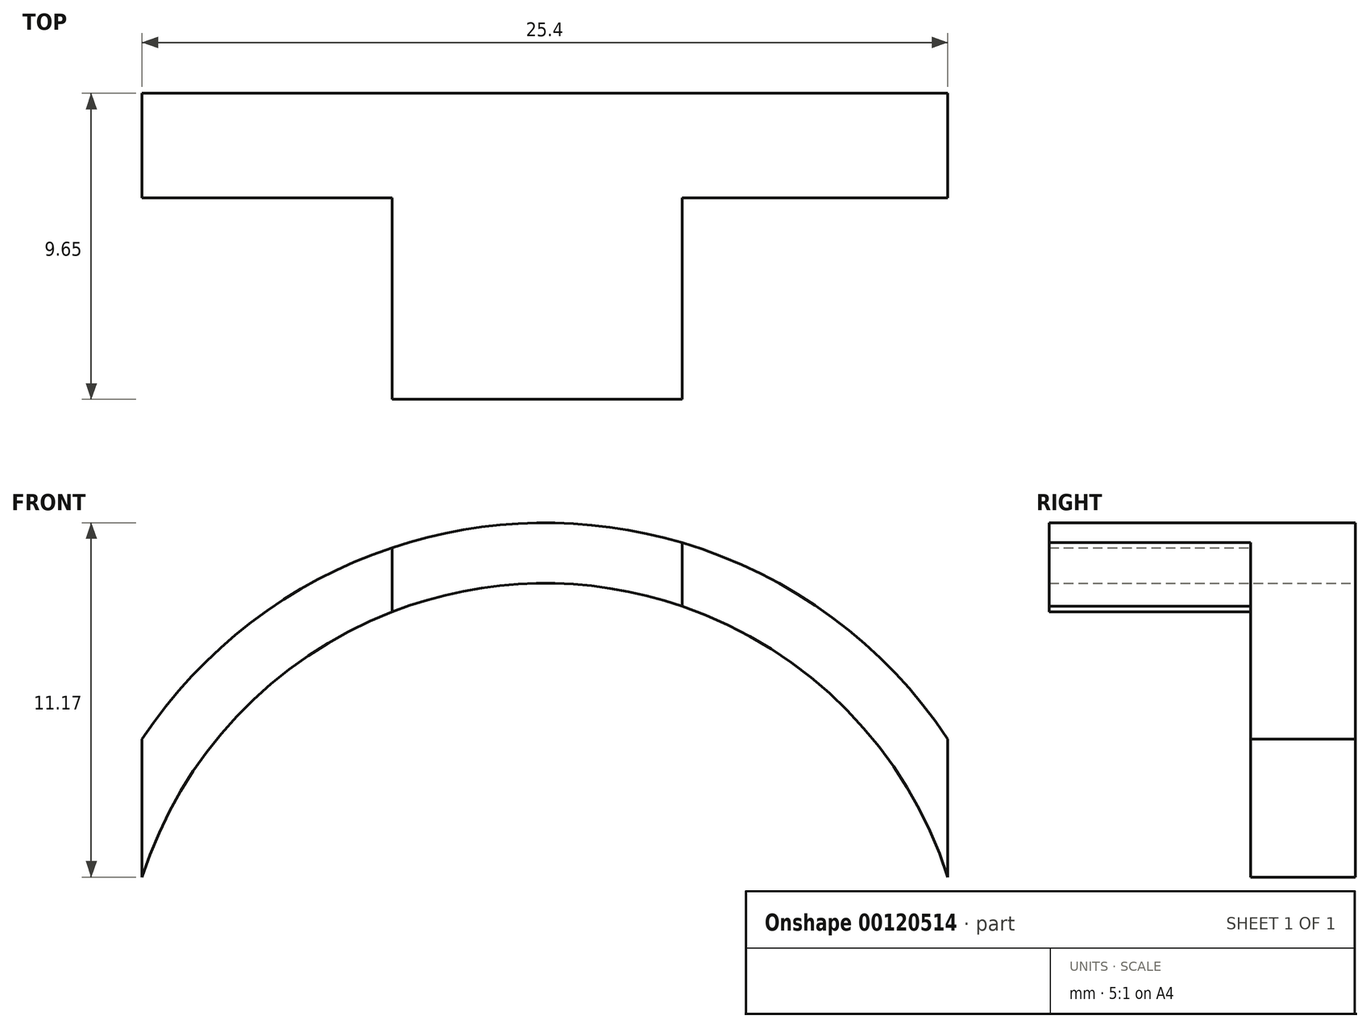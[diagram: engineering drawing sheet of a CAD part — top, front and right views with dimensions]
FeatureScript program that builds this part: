
annotation { "Feature Type Name" : "Feature", "Feature Type Description" : "" }
export const myFeature = defineFeature(function(context is Context, id is Id, definition is map)
    precondition{}
    {
        {
            var Q0;
            Q0=qCreatedBy(makeId("Front.planeOp"),FACE);
            var sketch = newSketch(context, id + "F0", { "sketchPlane" : qUnion([Q0])});
            skCircle(sketch, "E0", {"center": v(0, 0) * mm, "radius": 15.24 * mm});
            skCircle(sketch, "E1", {"center": v(0, 0) * mm, "radius": 13.34 * mm});
            skLineSegment(sketch, "E2.bottom", {"start": v(12.7, 0) * mm, "end": v(-12.7, 0) * mm});
            skLineSegment(sketch, "E2.top", {"start": v(12.7, 25.4) * mm, "end": v(-12.7, 25.4) * mm});
            skLineSegment(sketch, "E2.left", {"start": v(12.7, 0) * mm, "end": v(12.7, 25.4) * mm});
            skLineSegment(sketch, "E2.right", {"start": v(-12.7, 0) * mm, "end": v(-12.7, 25.4) * mm});
            skSolve(sketch);
        }
        {
            var Q0;
            {var subQ0=sQuery(id+"F0.wireOp",EDGE,"E2.left");var subQ1=sQuery(id+"F0.wireOp",EDGE,"E0");var subQ2=makeQuery(id+"F0.imprint","INTERSECT",VERTEX,{"derivedFrom":[subQ1,subQ0]});Q0=makeQuery(id+"F0.imprint","IMPRINT",FACE,{"disambiguationData":[TD([[makeQuery(id+"F0.imprint","IMPRINT",EDGE,{"disambiguationData":[TD([[subQ2,-1.0]])],"derivedFrom":subQ1}),1.0]])]});}
            extrude(context, id + "F1", {"entities" : qUnion([Q0]), "depth" : 3.3 * mm});
        }
        {
            var Q0;
            Q0=makeQuery(id+"F1.opExtrude","CAP_FACE",FACE,{"disambiguationData":[OSD([sQuery(id+"F0.wireOp",EDGE,"E0"),sQuery(id+"F0.wireOp",EDGE,"E1"),sQuery(id+"F0.wireOp",EDGE,"E2.left"),sQuery(id+"F0.wireOp",EDGE,"E2.right")])],"isStart":false});
            var sketch = newSketch(context, id + "F2", { "sketchPlane" : qUnion([Q0])});
            skLineSegment(sketch, "E3.bottom", {"start": v(-4.82, 15.24) * mm, "end": v(4.32, 15.24) * mm});
            skLineSegment(sketch, "E3.top", {"start": v(-4.82, -9.06) * mm, "end": v(4.32, -9.06) * mm});
            skLineSegment(sketch, "E3.left", {"start": v(-4.82, 15.24) * mm, "end": v(-4.82, -9.06) * mm});
            skLineSegment(sketch, "E3.right", {"start": v(4.32, 15.24) * mm, "end": v(4.32, -9.06) * mm});
            skSolve(sketch);
        }
        {
            var Q0;
            {var subQ0=makeQuery(id+"F1.opExtrude","CAP_EDGE",EDGE,{"disambiguationData":[OSD([sQuery(id+"F0.wireOp",EDGE,"E0")])],"isStart":false});var subQ2=sQuery(id+"F2.wireOp",EDGE,"E3.left");var subQ3=makeQuery(id+"F2.imprint","INTERSECT",VERTEX,{"derivedFrom":[subQ0,subQ2]});Q0=makeQuery(id+"F2.imprint","IMPRINT",FACE,{"disambiguationData":[TD([[makeQuery(id+"F2.imprint","IMPRINT",EDGE,{"disambiguationData":[TD([[subQ3,-1.0]])],"derivedFrom":subQ2}),1.0]])]});}
            extrude(context, id + "F3", {"entities" : qUnion([Q0]), "operationType" : NewBodyOperationType.ADD, "depth" : 6.35 * mm});
        }
    });
